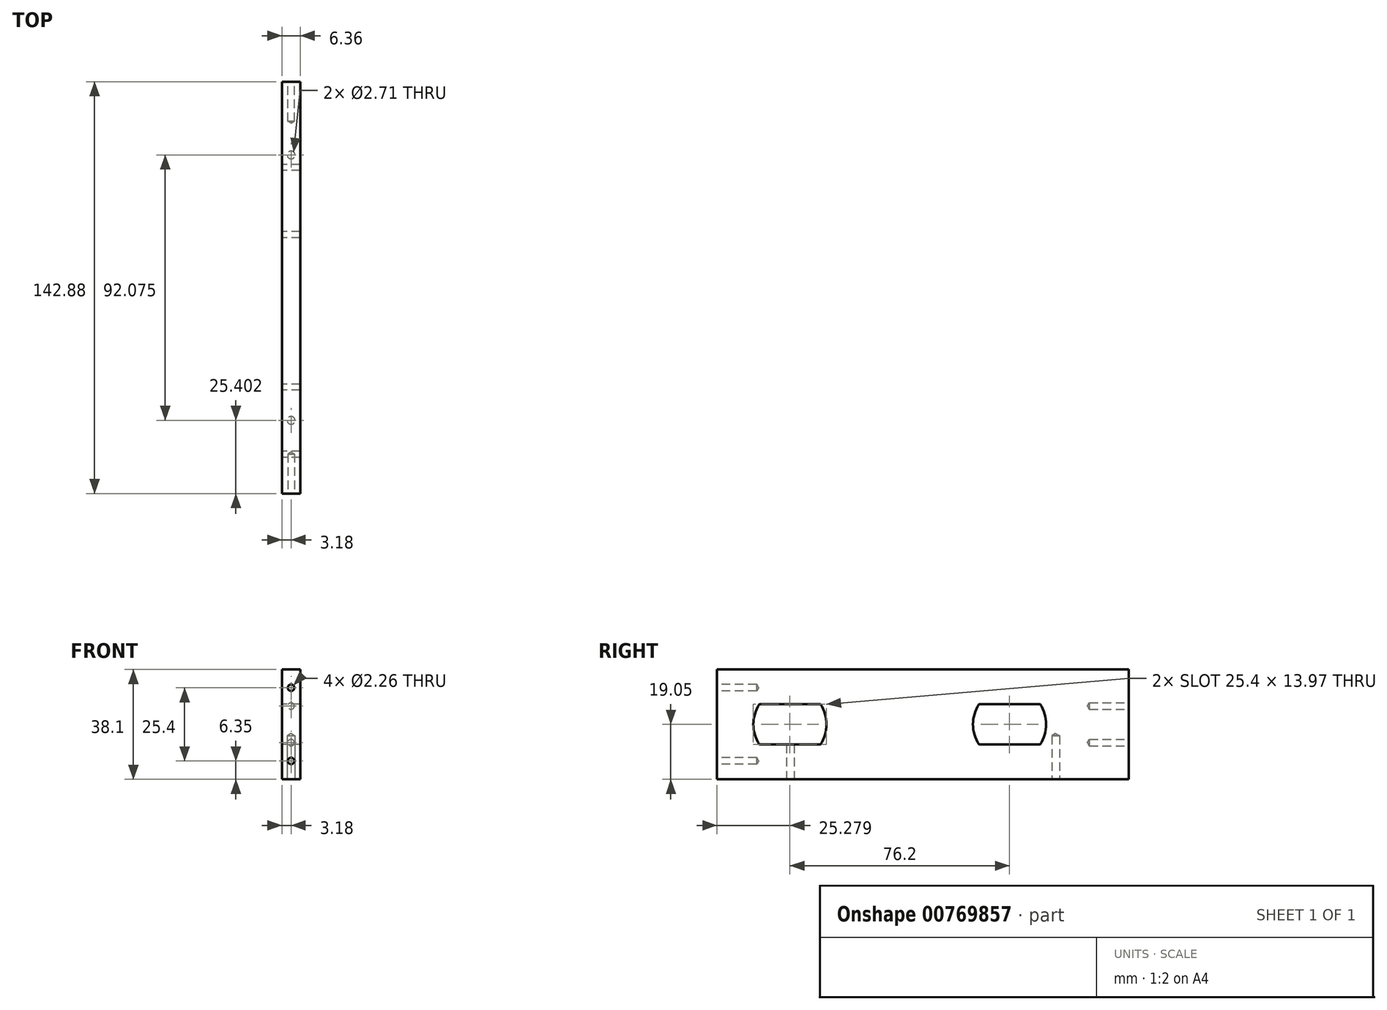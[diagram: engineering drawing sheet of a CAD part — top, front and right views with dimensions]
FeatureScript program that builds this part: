
annotation { "Feature Type Name" : "Feature", "Feature Type Description" : "" }
export const myFeature = defineFeature(function(context is Context, id is Id, definition is map)
    precondition{}
    {
        {
            var Q0;
            Q0=qCreatedBy(makeId("Top.planeOp"),FACE);
            var sketch = newSketch(context, id + "F0", { "sketchPlane" : qUnion([Q0])});
            skLineSegment(sketch, "E0.bottom", {"start": v(-3.17, 71.44) * mm, "end": v(3.18, 71.44) * mm});
            skLineSegment(sketch, "E0.top", {"start": v(-3.18, -71.44) * mm, "end": v(3.17, -71.44) * mm});
            skLineSegment(sketch, "E0.left", {"start": v(-3.17, 71.44) * mm, "end": v(-3.18, -71.44) * mm});
            skLineSegment(sketch, "E0.right", {"start": v(3.18, 71.44) * mm, "end": v(3.17, -71.44) * mm});
            skLineSegment(sketch, "E1", {"start": v(3.18, 71.44) * mm, "end": v(-3.18, -71.44) * mm, "construction": true});
            skSolve(sketch);
        }
        {
            var Q0;
            Q0 = qSketchRegion(id + "F0", true);
            extrude(context, id + "F1", {"entities" : qUnion([Q0]), "depth" : 38.1 * mm, "offsetDistance" : 25.4 * mm});
        }
        {
            var Q0;
            Q0=makeQuery(id+"F1.opExtrude","CAP_FACE",FACE,{"disambiguationData":[OSD([sQuery(id+"F0.wireOp",EDGE,"E0.bottom"),sQuery(id+"F0.wireOp",EDGE,"E0.top"),sQuery(id+"F0.wireOp",EDGE,"E0.left"),sQuery(id+"F0.wireOp",EDGE,"E0.right")])],"isStart":true});
            var sketch = newSketch(context, id + "F2", { "sketchPlane" : qUnion([Q0])});
            skLineSegment(sketch, "E2", {"start": v(0, 71.44) * mm, "end": v(0, -71.44) * mm, "construction": true});
            skPoint(sketch, "E3", {"position": v(0, 46.04) * mm});
            skPoint(sketch, "E4", {"position": v(0, -46.04) * mm});
            skSolve(sketch);
        }
        {
            var Q0;
            Q0=sQuery(id+"F2.wireOp",VERTEX,"E3");
            var Q1;
            Q1=sQuery(id+"F2.wireOp",VERTEX,"E4");
            var Q2;
            Q2=makeQuery(id+"F1.opExtrude","SWEPT_BODY",BODY,{"disambiguationData":[OSD([sQuery(id+"F0.wireOp",EDGE,"E0.bottom"),sQuery(id+"F0.wireOp",EDGE,"E0.top"),sQuery(id+"F0.wireOp",EDGE,"E0.left"),sQuery(id+"F0.wireOp",EDGE,"E0.right")])]});
            hole(context, id + "F3", {"style" : HoleStyle.SIMPLE, "endStyle" : HoleEndStyle.BLIND, "standardTappedOrClearance" : lookupTablePath({ "standard" : "ANSI", "engagement" : "75%", "pitch" : "32 tpi", "size" : "#6", "type" : "Tapped" }), "standardBlindInLast" : lookupTablePath({ "standard" : "ANSI", "engagement" : "75%", "pitch" : "32 tpi", "size" : "#6", "type" : "Tapped" }), "holeDiameter" : 2.7 * mm, "majorDiameter" : 3.5 * mm, "showTappedDepth" : true, "holeDepth" : 15.1 * mm, "tappedDepth" : 12.7 * mm, "tapClearance" : 3, "locations" : qUnion([Q0, Q1]), "scope" : qUnion([Q2])});
        }
        {
            var Q0;
            Q0=makeQuery(id+"F1.opExtrude","SWEPT_FACE",FACE,{"disambiguationData":[OSD([sQuery(id+"F0.wireOp",EDGE,"E0.bottom")])]});
            var sketch = newSketch(context, id + "F4", { "sketchPlane" : qUnion([Q0])});
            skLineSegment(sketch, "E5", {"start": v(0, 38.1) * mm, "end": v(0, 0) * mm, "construction": true});
            skPoint(sketch, "E6", {"position": v(0, 25.4) * mm});
            skPoint(sketch, "E7", {"position": v(0, 12.7) * mm});
            skPoint(sketch, "E8", {"position": v(0, 19.05) * mm});
            skSolve(sketch);
        }
        {
            var Q0;
            Q0=makeQuery(id+"F1.opExtrude","SWEPT_FACE",FACE,{"disambiguationData":[OSD([sQuery(id+"F0.wireOp",EDGE,"E0.top")])]});
            var sketch = newSketch(context, id + "F5", { "sketchPlane" : qUnion([Q0])});
            skLineSegment(sketch, "E9", {"start": v(0, 38.1) * mm, "end": v(0, 0) * mm, "construction": true});
            skPoint(sketch, "E10", {"position": v(0, 31.75) * mm});
            skPoint(sketch, "E11", {"position": v(0, 6.35) * mm});
            skPoint(sketch, "E12", {"position": v(0, 19.05) * mm});
            skSolve(sketch);
        }
        {
            var Q0;
            Q0=sQuery(id+"F5.wireOp",VERTEX,"E10");
            var Q1;
            Q1=sQuery(id+"F5.wireOp",VERTEX,"E11");
            var Q2;
            Q2=sQuery(id+"F4.wireOp",VERTEX,"E6");
            var Q3;
            Q3=sQuery(id+"F4.wireOp",VERTEX,"E7");
            var Q4;
            Q4=makeQuery(id+"F1.opExtrude","SWEPT_BODY",BODY,{"disambiguationData":[OSD([sQuery(id+"F0.wireOp",EDGE,"E0.bottom"),sQuery(id+"F0.wireOp",EDGE,"E0.top"),sQuery(id+"F0.wireOp",EDGE,"E0.left"),sQuery(id+"F0.wireOp",EDGE,"E0.right")])]});
            hole(context, id + "F6", {"style" : HoleStyle.SIMPLE, "endStyle" : HoleEndStyle.BLIND, "standardTappedOrClearance" : lookupTablePath({ "standard" : "ANSI", "engagement" : "75%", "pitch" : "40 tpi", "size" : "#4", "type" : "Tapped" }), "standardBlindInLast" : lookupTablePath({ "standard" : "ANSI", "engagement" : "75%", "pitch" : "40 tpi", "size" : "#4", "type" : "Tapped" }), "holeDiameter" : 2.26 * mm, "majorDiameter" : 2.84 * mm, "showTappedDepth" : true, "holeDepth" : 13.74 * mm, "tappedDepth" : 11.84 * mm, "tapClearance" : 3, "startFromSketch" : true, "locations" : qUnion([Q0, Q1, Q2, Q3]), "scope" : qUnion([Q4])});
        }
        {
            var Q0;
            Q0=makeQuery(id+"F1.opExtrude","SWEPT_FACE",FACE,{"disambiguationData":[OSD([sQuery(id+"F0.wireOp",EDGE,"E0.left")])]});
            var sketch = newSketch(context, id + "F7", { "sketchPlane" : qUnion([Q0])});
            skLineSegment(sketch, "E13", {"start": v(-71.44, 19.05) * mm, "end": v(71.44, 19.05) * mm, "construction": true});
            skLineSegment(sketch, "E14", {"start": v(0, 38.1) * mm, "end": v(0, 0) * mm, "construction": true});
            skArc(sketch, "E15", {"start": v(-40.65, 26.04) * mm, "mid": v(-42.74, 19.05) * mm, "end": v(-40.65, 12.07) * mm});
            skArc(sketch, "E16", {"start": v(56.77, 12.07) * mm, "mid": v(58.86, 19.05) * mm, "end": v(56.77, 26.04) * mm});
            skLineSegment(sketch, "E17.bottom", {"start": v(-40.65, 26.04) * mm, "end": v(-19.43, 26.04) * mm});
            skLineSegment(sketch, "E17.top", {"start": v(-40.65, 12.07) * mm, "end": v(-19.43, 12.07) * mm});
            skLineSegment(sketch, "E17.left", {"start": v(-40.65, 26.04) * mm, "end": v(-40.65, 12.07) * mm, "construction": true});
            skLineSegment(sketch, "E17.right", {"start": v(-19.43, 26.04) * mm, "end": v(-19.43, 12.07) * mm, "construction": true});
            skLineSegment(sketch, "E18.bottom", {"start": v(35.55, 26.04) * mm, "end": v(56.77, 26.04) * mm});
            skLineSegment(sketch, "E18.top", {"start": v(35.55, 12.07) * mm, "end": v(56.77, 12.07) * mm});
            skLineSegment(sketch, "E18.left", {"start": v(35.55, 26.04) * mm, "end": v(35.55, 12.07) * mm, "construction": true});
            skLineSegment(sketch, "E18.right", {"start": v(56.77, 26.04) * mm, "end": v(56.77, 12.07) * mm, "construction": true});
            skArc(sketch, "E19.trimOffspring", {"start": v(-19.43, 12.07) * mm, "mid": v(-17.34, 19.05) * mm, "end": v(-19.43, 26.04) * mm});
            skArc(sketch, "E20.trimOffspring", {"start": v(35.55, 26.04) * mm, "mid": v(33.46, 19.05) * mm, "end": v(35.55, 12.07) * mm});
            skSolve(sketch);
        }
        {
            var Q0;
            Q0 = qSketchRegion(id + "F7", true);
            extrude(context, id + "F8", {"entities" : qUnion([Q0]), "operationType" : NewBodyOperationType.REMOVE, "oppositeDirection" : true, "depth" : 25.4 * mm, "offsetDistance" : 25.4 * mm});
        }
    });
